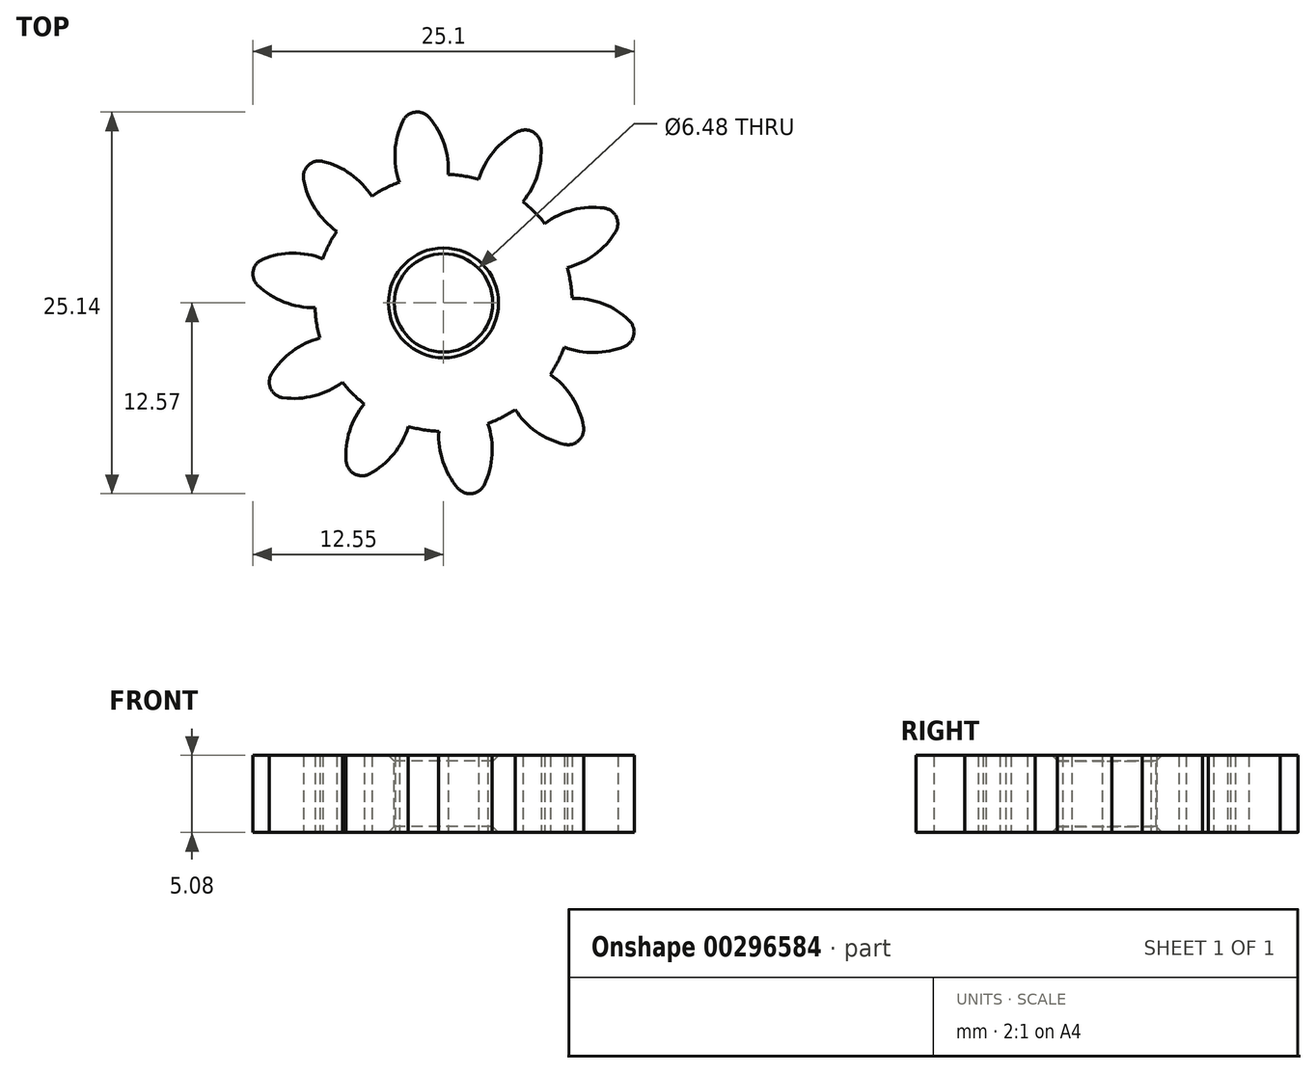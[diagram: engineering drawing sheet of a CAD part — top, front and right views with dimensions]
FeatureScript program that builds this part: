
annotation { "Feature Type Name" : "Feature", "Feature Type Description" : "" }
export const myFeature = defineFeature(function(context is Context, id is Id, definition is map)
    precondition{}
    {
        {
            var Q0;
            Q0=qCreatedBy(makeId("Top.planeOp"),FACE);
            var sketch = newSketch(context, id + "F0", { "sketchPlane" : qUnion([Q0])});
            skCircle(sketch, "E0", {"center": v(0, 0) * mm, "radius": 8.47 * mm});
            skCircle(sketch, "E1", {"center": v(0, 0) * mm, "radius": 10.58 * mm, "construction": true});
            skArc(sketch, "E2", {"start": v(-1.99, 12.54) * mm, "mid": v(1.4, -12.62) * mm, "end": v(-0.8, 12.67) * mm, "construction": true});
            skLineSegment(sketch, "E3", {"start": v(0, 0) * mm, "end": v(0, 10.58) * mm, "construction": true});
            skLineSegment(sketch, "E4", {"start": v(0, 10.58) * mm, "end": v(-24.86, 10.58) * mm, "construction": true});
            skLineSegment(sketch, "E5", {"start": v(0, 10.58) * mm, "end": v(-24.73, 1.58) * mm, "construction": true});
            skArc(sketch, "E6", {"start": v(0.3, 8.46) * mm, "mid": v(0.04, 10.46) * mm, "end": v(-0.95, 12.2) * mm});
            skArc(sketch, "E7.MirrorCS", {"start": v(-2.9, 7.95) * mm, "mid": v(-3.2, 10) * mm, "end": v(-2.67, 11.99) * mm});
            skLineSegment(sketch, "E8", {"start": v(0, 0) * mm, "end": v(-1.99, 12.54) * mm, "construction": true});
            skLineSegment(sketch, "E9", {"start": v(-2.9, 7.95) * mm, "end": v(-1.32, 8.36) * mm, "construction": true});
            skLineSegment(sketch, "E10", {"start": v(0.3, 8.46) * mm, "end": v(-1.32, 8.36) * mm, "construction": true});
            skLineSegment(sketch, "E11", {"start": v(-1.58, 10) * mm, "end": v(5.36, 9.4) * mm, "construction": true});
            skArc(sketch, "E12", {"start": v(-0.95, 12.2) * mm, "mid": v(-1.87, 12.57) * mm, "end": v(-2.67, 11.99) * mm});
            skSolve(sketch);
        }
        {
            var Q0;
            Q0 = qSketchRegion(id + "F0", true);
            extrude(context, id + "F1", {"entities" : qUnion([Q0]), "flatOperationType" : FlatOperationType.REMOVE, "offsetDistance" : 25.4 * mm, "depth" : 5.08 * mm, "domain" : OperationDomain.MODEL});
        }
        {
            var Q0;
            Q0=makeQuery(id+"F1.opExtrude","SWEPT_FACE",FACE,{"disambiguationData":[OSD([sQuery(id+"F0.wireOp",EDGE,"E7.MirrorCS")])]});
            var Q1;
            Q1=makeQuery(id+"F1.opExtrude","SWEPT_FACE",FACE,{"disambiguationData":[OSD([sQuery(id+"F0.wireOp",EDGE,"E12")])]});
            var Q2;
            Q2=makeQuery(id+"F1.opExtrude","SWEPT_FACE",FACE,{"disambiguationData":[OSD([sQuery(id+"F0.wireOp",EDGE,"E6")])]});
            var Q3;
            Q3=makeQuery(id+"F1.opExtrude","SWEPT_FACE",FACE,{"disambiguationData":[OSD([sQuery(id+"F0.wireOp",EDGE,"E0")])]});
            circularPattern(context, id + "F2", {"patternType" : PatternType.FACE, "faces" : qUnion([Q0, Q1, Q2]), "axis" : qUnion([Q3]), "angle" : 360 * degree, "instanceCount" : 10, "equalSpace" : true, "fullFeaturePattern" : false});
        }
        {
            var Q0;
            Q0=makeQuery(id+"F1.opExtrude","CAP_FACE",FACE,{"disambiguationData":[OSD([sQuery(id+"F0.wireOp",EDGE,"E0"),sQuery(id+"F0.wireOp",EDGE,"E6"),sQuery(id+"F0.wireOp",EDGE,"E7.MirrorCS"),sQuery(id+"F0.wireOp",EDGE,"lxTbqiqL-FpUp-zF25-s7r9-AZY9gUb4hh0W")])],"isStart":false});
            var sketch = newSketch(context, id + "F3", { "sketchPlane" : qUnion([Q0])});
            skCircle(sketch, "E13", {"center": v(0, 0) * mm, "radius": 3.24 * mm});
            skSolve(sketch);
        }
        {
            var Q0;
            Q0 = qSketchRegion(id + "F3", true);
            extrude(context, id + "F4", {"entities" : qUnion([Q0]), "operationType" : NewBodyOperationType.REMOVE, "oppositeDirection" : true, "depth" : 25.4 * mm});
        }
        {
            var Q0;
            Q0=makeQuery(id+"F4.boolean.opBoolean","COPY",FACE,{"derivedFrom":makeQuery(id+"F4.opExtrude","SWEPT_FACE",FACE,{"disambiguationData":[OSD([sQuery(id+"F3.wireOp",EDGE,"E13")])]})});
            chamfer(context, id + "F5", {"entities" : qUnion([Q0]), "width" : 0.38 * mm, "tangentPropagation" : true});
        }
    });
